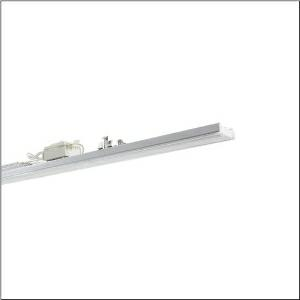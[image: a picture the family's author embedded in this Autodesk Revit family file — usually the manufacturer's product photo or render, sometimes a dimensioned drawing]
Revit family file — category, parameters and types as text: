
# Revit family: licross_r__21_recessed_mo_52tl12dn4axg3s4_bc26
name_source: partatom
category: Lighting Fixtures
units: mm (PartAtom-declared; Revit-internal decimal feet)

## family parameters
Cut with Voids When Loaded = No
Host = Face
Light Source = No
Part Type = Normal
Room Calculation Point = No
Round Connector Dimension = Use Diameter
Shared = No

## types (1)
- --- (1 x LED, 950 lm, 6.7 W, 4000K)
    Apparent Load = 7 VA
    CIE Flux Codes = 72 92 99 100 100
    Color Rendering = 80
    Color Temperature = 4000K
    Default Elevation = 1800 mm
    Description = Licross® 21 Recessed MO, luminaire insert, of sheet steel, galvanised, coil coated, white, length: 1.500mm, width: 66mm, height: 67mm, LED rated luminous flux: 10.280lm, light colour: 840, control gear: DALI 2, with plug, 6-pole, with phase selection, for trunking rail, 9 or 11-core, mains connection: 220..240V, AC, 50/60Hz, rated input power: 62W, for trunking rail, 9-/11-core, halogen-free wiring, for emergency light function, converter,control gear: single battery element, battery: LiFePO4, 9Ah, primary optical cover: cover, of PMMA, light emission: direct distribution, primary light characteristic: symmetric, protection rating (complete): IP40, insulation class (complete): insulation class I (protective earthing), certification: CE, UKCA, protection symbol: D if used in an environment without relevant dust loads with corresponding accessories, impact resistance: IK06, permissible ambient temperature for indoor applications: +5..+35°C, standard: EN 60598-2-22, LABS conformity tested according to VDMA 24364:2018-05, reducing of maximum allowable ambient temperature of 5°C with ceiling mounting, corresponds to IFS (International Featured Standards) requirements for safety and quality in the food industry, packaging unit: 1 piece
    Height = 58 mm
    Lamp = 1 x LED
    Lamp Light Flux = 950 lm
    Lamp Power = 6.7 W
    Lamp count = 1
    Length = 1500 mm
    Luminous efficacy = 142 lm/W
    Manufacturer = Siteco
    ModVariant = No
    Model = 52TL12DN4AXG3S4
    Mounting Place = Ceiling
    Mounting Type = Pendant
    Number of Poles = 1
    OnlyDefault = Yes
    Power Factor = 1
    Product Name = Licross® 21 Recessed MO
    Product group = luminaire insert
    ProductGroupID = 902
    Protection Class = Protection class I
    Protection Degree = IP 40
    RLX_Detail_Level = 1
    RLX_Emergency_Light_Flux = 0 lm
    RLX_Emergency_Type = 0
    RLX_Emergency_Type_DB = No
    RlxData = <blob elided: 25029 chars, md5=17746054>
    Socket = socket
    Standby Power = 0 W
    System Light Flux = 950 lm
    System Power = 7 W
    Type Comments = : emergency light operation: 3 h
    Type Image = l_1296930.jpg
    URL = http://relux.com
    VarID = @adj_110052
    Voltage = 0 V
    Weight = 0.00 kg
    Width = 66 mm

## geometry (parser evidence)
native form markers: Blend x4, Sweep x9
no freeform markers — native parametric forms only
